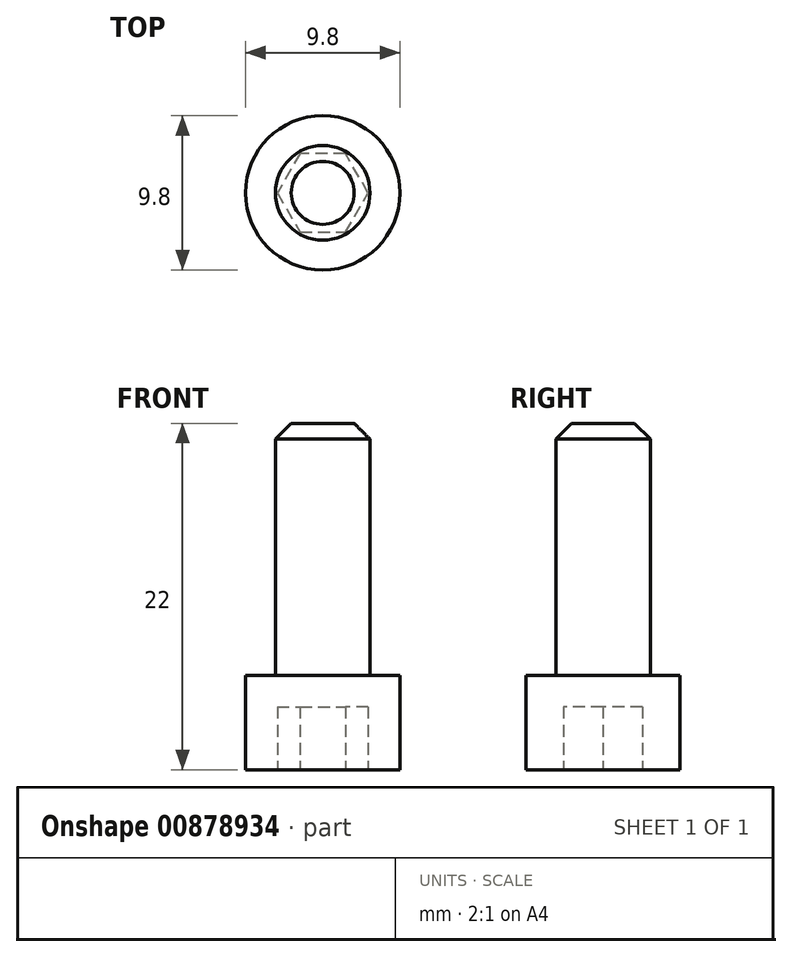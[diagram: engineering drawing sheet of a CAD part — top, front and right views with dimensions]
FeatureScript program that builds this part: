
annotation { "Feature Type Name" : "Feature", "Feature Type Description" : "" }
export const myFeature = defineFeature(function(context is Context, id is Id, definition is map)
    precondition{}
    {
        {
            var Q0;
            Q0=qCreatedBy(makeId("Top.planeOp"),FACE);
            var sketch = newSketch(context, id + "F0", { "sketchPlane" : qUnion([Q0])});
            skCircle(sketch, "E0", {"center": v(0, 0) * mm, "radius": 3 * mm});
            skSolve(sketch);
        }
        {
            var Q0;
            Q0=makeQuery(id+"F0.imprint","IMPRINT",FACE,{"disambiguationData":[TD([[makeQuery(id+"F0.imprint","IMPRINT",EDGE,{"derivedFrom":sQuery(id+"F0.wireOp",EDGE,"E0")}),1.0]])]});
            extrude(context, id + "F1", {"entities" : qUnion([Q0]), "depth" : 16 * mm, "offsetDistance" : 25 * mm});
        }
        {
            var Q0;
            Q0=makeQuery(id+"F1.opExtrude","CAP_FACE",FACE,{"disambiguationData":[OSD([sQuery(id+"F0.wireOp",EDGE,"E0")])],"isStart":true});
            var sketch = newSketch(context, id + "F2", { "sketchPlane" : qUnion([Q0])});
            skCircle(sketch, "E1", {"center": v(0, 0) * mm, "radius": 4.9 * mm});
            skSolve(sketch);
        }
        {
            var Q0;
            Q0 = qSketchRegion(id + "F2", true);
            extrude(context, id + "F3", {"entities" : qUnion([Q0]), "operationType" : NewBodyOperationType.ADD, "depth" : 6 * mm, "offsetDistance" : 25 * mm});
        }
        {
            var Q0;
            Q0=makeQuery(id+"F3.opExtrude","CAP_FACE",FACE,{"disambiguationData":[OSD([sQuery(id+"F2.wireOp",EDGE,"E1")])],"isStart":false});
            var sketch = newSketch(context, id + "F4", { "sketchPlane" : qUnion([Q0])});
            skCircle(sketch, "E2.cCircle", {"center": v(0, 0) * mm, "radius": 2.5 * mm, "construction": true});
            skLineSegment(sketch, "E2.0", {"start": v(-1.44, 2.5) * mm, "end": v(1.44, 2.5) * mm});
            skLineSegment(sketch, "E2.1", {"start": v(1.44, 2.5) * mm, "end": v(2.89, 0) * mm});
            skLineSegment(sketch, "E2.2", {"start": v(2.89, 0) * mm, "end": v(1.44, -2.5) * mm});
            skLineSegment(sketch, "E2.3", {"start": v(1.44, -2.5) * mm, "end": v(-1.44, -2.5) * mm});
            skLineSegment(sketch, "E2.4", {"start": v(-1.44, -2.5) * mm, "end": v(-2.89, 0) * mm});
            skLineSegment(sketch, "E2.5", {"start": v(-2.89, 0) * mm, "end": v(-1.44, 2.5) * mm});
            skPoint(sketch, "E2.0.midPoint", {"position": v(0, 2.5) * mm});
            skSolve(sketch);
        }
        {
            var Q0;
            Q0 = qSketchRegion(id + "F4", true);
            extrude(context, id + "F5", {"entities" : qUnion([Q0]), "operationType" : NewBodyOperationType.REMOVE, "oppositeDirection" : true, "depth" : 4 * mm, "offsetDistance" : 25 * mm});
        }
        {
            var Q0;
            Q0=makeQuery(id+"F1.opExtrude","CAP_EDGE",EDGE,{"disambiguationData":[OSD([sQuery(id+"F0.wireOp",EDGE,"E0")])],"isStart":false});
            chamfer(context, id + "F6", {"entities" : qUnion([Q0]), "width" : 1 * mm, "tangentPropagation" : true});
        }
    });
